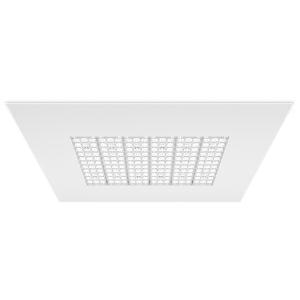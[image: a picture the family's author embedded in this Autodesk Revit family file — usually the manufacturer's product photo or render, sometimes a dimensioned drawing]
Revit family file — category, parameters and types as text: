
# Revit family: 3f_filippi_-_3f_six_r_ampio_3f_filippi_-_22232_-_3f_six_r_60-840_wide_596x596
name_source: partatom
category: Lighting Fixtures
units: mm (PartAtom-declared; Revit-internal decimal feet)

## family parameters
Cut with Voids When Loaded = No
Host = Face
Light Source = No
Part Type = Normal
Room Calculation Point = No
Round Connector Dimension = Use Diameter
Shared = No

## types (1)
- 3F Filippi - 3F Six R Ampio (1 x LED, 9530 lm, 55.5 W, 4000 K)
    Apparent Load = 56 VA
    Approval mark = ENEC
    CIE Flux Codes = 61 95 99 100 100
    Color Rendering = 80
    Color Temperature = 4000 K
    Control Gear = Electronic ballast
    Default Elevation = 1800 mm
    Description = ILLUMINOTECHNICAL
Luminous efficiency 100% (DLOR 100%, ULOR 0%).
Initial luminous flux of the luminaire 9530 lm.
Direct symmetric distribution.
Installation Interdistance Transv.D = 1.39 x hu - Long.D = 1.43 x hu.
Tabular UGR (CIE 117 - 4H-8H; S=0.25H; 70/50/20): RUG 22.9 - 23.2.
Beam angle: 102° - 103°.
Luminous efficacy 172 lm/W.
Lifetime (L93/B10): 30000 h. (tq+25°C)
Lifetime (L90/B10): 50000 h. (tq+25°C)
Lifetime (L85/B10): 80000 h. (tq+25°C)
Lifetime (L80/B10): 100000 h. (tq+25°C)
Lifetime (L85/B10): 50000 h. (tq+40°C)
Sudden decreased luminous flux after 50000 hours: 0% (C0).
Photobiological safety in compliance with IEC/TR 62778: RG0 risk exempt, (IEC 62471).
In compliance with IEC/EN 62722-2-1 - IEC/EN 62717 standards.

SOURCE
Linear LED module 60W/840.
Energy efficiency class (UE 2019/2020 - UE 2019/2015): C.
CIE 13.3 Colour rendering index: CRI >80 (R9 <50%).
IES TM-30 Fidelity Index: Rf = 84 Rg = 95.
CCT nominal colour temperature 4000 K.
Colour initial tolerance (MacAdam): SDCM 3.

MECHANICAL
Housing in galvannealed steel, painted in white epoxy-polyester.
Methacrylate (PMMA) lenses with external flat surface.
Luminaire with limited surface temperature. - D - (EN 60598-2-24)
Dimensions: 596x596 mm, height 70 mm. Weight 4.525 kg.
IP40 protection degree.
Mechanical strength to impacts IK06 (1 joule).
Glow-wire test resistance 650°C.

ELECTRICAL
Halogen Free electronic wiring 230V-50/60Hz, power factor 0.97, THD <25%, constant output current, class I, 1 driver.
Power of the luminaire 55.5 W.
CE - IEC 60598-1 - EN 60598-1.
SAFE FLICKER: PstLM=<1 and SVM=<0.4 (IEC TR 61547-1 and IEC TR 63158), to ensure a more comfortable and safe light.
Luminaire compliant with EN 60598-2-22 for power supply from a centralised emergency system CPSS (Central Power Supply System), not incorporated in the luminaire - high risk areas excluded. The default power and flux are 100% in AC and 100% in DC.
Ambient temperature from 0°C to +40°C.
Temperature class T6 max 85°C.
Power cable type H05Z1Z1-F 3x1,5 mm² that protrudes by 1 m with sheared ends.
Relative humidity UR: <85%.

INSTALLATION
Lay-in recessed fitting.
All accessories dedicated to this product are available on the Catalog and on our website www.3F-Filippi.com.

APPLICATIONS
Suitable product for food production plants (HACCP), IFS (Food Version 6), BRC (GSFS Food Version 7).
Environments: commercial, exhibition areas, transit areas, lobbies or waiting rooms, shops.

WARNING
Luminaire designed for disposal/recycling at end-of-life.
Replaceable (LED only) light source by a professional. Replaceable control gear by a professional.
    Height = 0 mm  [stored 0 ft]
    Lamp = 1 x LED
    Lamp Light Flux = 9530 lm
    Lamp Power = 55.5 W
    Lamp count = 1
    Length = 596 mm
    Lifetime = 50000 h
    Luminous efficacy = 172 lm/W
    Manufacturer = 3F Filippi
    ModVariant = No
    Model = 3F Filippi - 22232 - 3F Six R 60-840 WIDE 596x596
    Mounting Place = Ceiling
    Mounting Type = Recessed
    Number of Poles = 1
    OnlyDefault = Yes
    Power Factor = 1
    Product Name = 3F Filippi - 3F Six R Ampio
    Product group = recessed luminaire
    ProductGroupID = 4
    Protection Class = Protection class I
    Protection Degree = IP 40
    RLX_Detail_Level = 1
    RLX_Emergency_Light_Flux = 0 lm
    RLX_Emergency_Type = 0
    RLX_Emergency_Type_DB = No
    RlxData = <blob elided: 127633 chars, md5=723c4b84>
    Socket = socket
    Standby Power = 0 W
    System Light Flux = 9530 lm
    System Power = 56 W
    Type Comments = Product without accessories
    Type Image = 3ffilippi_3f_six_r_ampio.jpg
    URL = http://relux.com
    VarID = ---
    Voltage = 0 V
    Weight = 0.00 kg
    Width = 596 mm

note: [stored X ft] marks values corroborated as IEEE doubles in the binary element streams (Revit-internal decimal feet)

## geometry (parser evidence)
native form markers: Blend x4, Sweep x11
no freeform markers — native parametric forms only
